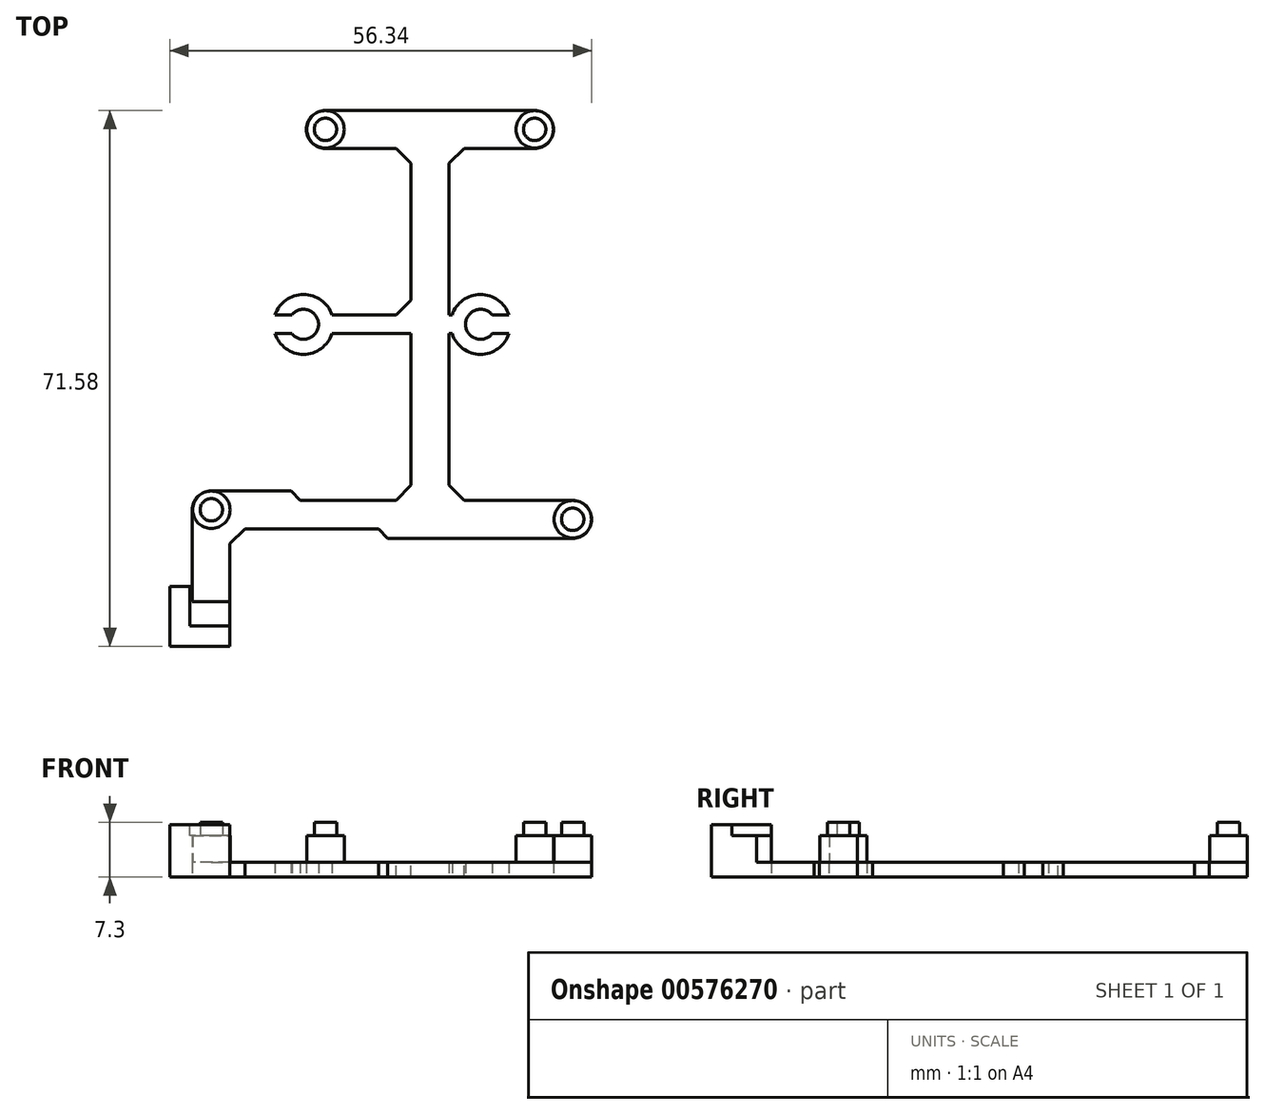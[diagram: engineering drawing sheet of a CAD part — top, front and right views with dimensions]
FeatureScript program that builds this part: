
annotation { "Feature Type Name" : "Feature", "Feature Type Description" : "" }
export const myFeature = defineFeature(function(context is Context, id is Id, definition is map)
    precondition{}
    {
        {
            var Q0;
            Q0=qCreatedBy(makeId("Top.planeOp"),FACE);
            var sketch = newSketch(context, id + "F0", { "sketchPlane" : qUnion([Q0])});
            skCircle(sketch, "E0", {"center": v(0, 0) * mm, "radius": 1.5 * mm, "construction": true});
            skLineSegment(sketch, "E1", {"start": v(2.46, -2.54) * mm, "end": v(2.46, -15.24) * mm});
            skLineSegment(sketch, "E2", {"start": v(2.46, -15.24) * mm, "end": v(-2.54, -15.24) * mm});
            skLineSegment(sketch, "E3", {"start": v(-2.54, -15.24) * mm, "end": v(-2.54, 0) * mm});
            skArc(sketch, "E4", {"start": v(0, 2.54) * mm, "mid": v(-1.8, 1.8) * mm, "end": v(-2.54, 0) * mm});
            skLineSegment(sketch, "E5", {"start": v(-2.54, -15.24) * mm, "end": v(-2.54, 45.8) * mm, "construction": true});
            skCircle(sketch, "E6", {"center": v(48.26, -1.27) * mm, "radius": 1.5 * mm, "construction": true});
            skCircle(sketch, "E7", {"center": v(15.24, 50.8) * mm, "radius": 1.5 * mm, "construction": true});
            skCircle(sketch, "E8", {"center": v(43.18, 50.8) * mm, "radius": 1.5 * mm, "construction": true});
            skLineSegment(sketch, "E9", {"start": v(15.24, 50.8) * mm, "end": v(43.18, 50.8) * mm, "construction": true});
            skArc(sketch, "E10", {"start": v(48.26, -3.8) * mm, "mid": v(50.8, -1.27) * mm, "end": v(48.26, 1.27) * mm});
            skLineSegment(sketch, "E11", {"start": v(0, 2.54) * mm, "end": v(10.66, 2.54) * mm});
            skLineSegment(sketch, "E12", {"start": v(48.26, 1.27) * mm, "end": v(31.75, 1.27) * mm});
            skLineSegment(sketch, "E13", {"start": v(10.66, 2.54) * mm, "end": v(11.85, 1.27) * mm});
            skLineSegment(sketch, "E14.0", {"start": v(22.36, -2.54) * mm, "end": v(23.55, -3.8) * mm});
            skLineSegment(sketch, "E14.1", {"start": v(48.26, -3.8) * mm, "end": v(23.55, -3.8) * mm});
            skLineSegment(sketch, "E15", {"start": v(22.36, -2.54) * mm, "end": v(2.46, -2.54) * mm});
            skLineSegment(sketch, "E16", {"start": v(29.21, 50.8) * mm, "end": v(29.21, -4.9) * mm, "construction": true});
            skArc(sketch, "E17", {"start": v(15.24, 53.34) * mm, "mid": v(12.7, 50.8) * mm, "end": v(15.24, 48.26) * mm});
            skArc(sketch, "E18", {"start": v(43.18, 48.26) * mm, "mid": v(45.72, 50.8) * mm, "end": v(43.18, 53.34) * mm});
            skLineSegment(sketch, "E19", {"start": v(15.24, 53.34) * mm, "end": v(43.18, 53.34) * mm});
            skLineSegment(sketch, "E20", {"start": v(26.67, 48.26) * mm, "end": v(26.67, 1.27) * mm});
            skLineSegment(sketch, "E21.MirrorCS", {"start": v(31.75, 48.26) * mm, "end": v(31.75, 1.27) * mm});
            skLineSegment(sketch, "E22", {"start": v(15.24, 48.26) * mm, "end": v(26.67, 48.26) * mm});
            skPoint(sketch, "E23.orphan", {"position": v(26.67, 50.02) * mm});
            skPoint(sketch, "E24.orphan", {"position": v(31.75, 50.02) * mm});
            skLineSegment(sketch, "E25.trimOffspring", {"start": v(31.75, 48.26) * mm, "end": v(43.18, 48.26) * mm});
            skPoint(sketch, "E26.orphan", {"position": v(26.67, 1.3) * mm});
            skLineSegment(sketch, "E27.trimOffspring", {"start": v(26.67, 1.27) * mm, "end": v(11.85, 1.27) * mm});
            skPoint(sketch, "E28.orphan", {"position": v(31.75, 1.3) * mm});
            skSolve(sketch);
        }
        {
            var Q0;
            Q0=makeQuery(id+"F0.imprint","IMPRINT",FACE,{"disambiguationData":[TD([[makeQuery(id+"F0.imprint","IMPRINT",EDGE,{"derivedFrom":sQuery(id+"F0.wireOp",EDGE,"E0")}),-1.0]])]});
            var Q1;
            Q1=makeQuery(id+"F0.imprint","IMPRINT",FACE,{"disambiguationData":[TD([[makeQuery(id+"F0.imprint","IMPRINT",EDGE,{"derivedFrom":sQuery(id+"F0.wireOp",EDGE,"jqxbBATG-ABpr-iL7b-bOAr-Zq2woUx4JpKi")}),1.0]])]});
            var Q2;
            Q2=makeQuery(id+"F0.imprint","IMPRINT",FACE,{"disambiguationData":[TD([[makeQuery(id+"F0.imprint","IMPRINT",EDGE,{"derivedFrom":sQuery(id+"F0.wireOp",EDGE,"E1")}),-1.0]])]});
            extrude(context, id + "F1", {"entities" : qUnion([Q0, Q1, Q2]), "depth" : 2 * mm, "offsetDistance" : 25 * mm});
        }
        {
            var Q0;
            Q0=qCreatedBy(makeId("Top.planeOp"),FACE);
            var sketch = newSketch(context, id + "F2", { "sketchPlane" : qUnion([Q0])});
            skLineSegment(sketch, "E29.0", {"start": v(-2.54, -15.24) * mm, "end": v(-2.54, 0) * mm, "construction": true});
            skLineSegment(sketch, "E30.0", {"start": v(2.46, -15.24) * mm, "end": v(-2.54, -15.24) * mm});
            skLineSegment(sketch, "E31", {"start": v(-2.54, -15.24) * mm, "end": v(-2.54, -10.24) * mm});
            skLineSegment(sketch, "E32", {"start": v(-2.54, -10.24) * mm, "end": v(-5.54, -10.24) * mm});
            skLineSegment(sketch, "E33", {"start": v(-5.54, -10.24) * mm, "end": v(-5.54, -18.24) * mm});
            skLineSegment(sketch, "E34", {"start": v(-5.54, -18.24) * mm, "end": v(2.46, -18.24) * mm});
            skLineSegment(sketch, "E35", {"start": v(2.46, -15.24) * mm, "end": v(2.46, -18.24) * mm});
            skSolve(sketch);
        }
        {
            var Q0;
            Q0=makeQuery(id+"F2.imprint","IMPRINT",FACE,{"disambiguationData":[TD([[makeQuery(id+"F2.imprint","IMPRINT",EDGE,{"derivedFrom":sQuery(id+"F2.wireOp",EDGE,"E30.0")}),1.0]])]});
            extrude(context, id + "F3", {"entities" : qUnion([Q0]), "operationType" : NewBodyOperationType.ADD, "depth" : 7 * mm, "offsetDistance" : 25 * mm});
        }
        {
            var Q0;
            Q0=qCreatedBy(makeId("Top.planeOp"),FACE);
            var sketch = newSketch(context, id + "F4", { "sketchPlane" : qUnion([Q0])});
            skCircle(sketch, "E36.0", {"center": v(0, 0) * mm, "radius": 1.5 * mm, "construction": true});
            skCircle(sketch, "E37.0", {"center": v(48.26, -1.27) * mm, "radius": 1.5 * mm, "construction": true});
            skCircle(sketch, "E38.0", {"center": v(43.18, 50.8) * mm, "radius": 1.5 * mm, "construction": true});
            skCircle(sketch, "E39.0", {"center": v(15.24, 50.8) * mm, "radius": 1.5 * mm, "construction": true});
            skCircle(sketch, "E40", {"center": v(0, 0) * mm, "radius": 2.5 * mm});
            skCircle(sketch, "E41", {"center": v(48.26, -1.27) * mm, "radius": 2.5 * mm});
            skCircle(sketch, "E42", {"center": v(15.24, 50.8) * mm, "radius": 2.5 * mm});
            skCircle(sketch, "E43", {"center": v(43.18, 50.8) * mm, "radius": 2.5 * mm});
            skLineSegment(sketch, "E44.0", {"start": v(-2.54, -15.24) * mm, "end": v(-2.54, -10.24) * mm, "construction": true});
            skLineSegment(sketch, "E45.0", {"start": v(2.46, -15.24) * mm, "end": v(-2.54, -15.24) * mm, "construction": true});
            skLineSegment(sketch, "E46.bottom", {"start": v(-2.54, -15.24) * mm, "end": v(2.46, -15.24) * mm});
            skLineSegment(sketch, "E46.top", {"start": v(-2.54, -12.24) * mm, "end": v(2.46, -12.24) * mm});
            skLineSegment(sketch, "E46.left", {"start": v(-2.54, -15.24) * mm, "end": v(-2.54, -12.24) * mm});
            skLineSegment(sketch, "E46.right", {"start": v(2.46, -15.24) * mm, "end": v(2.46, -12.24) * mm});
            skSolve(sketch);
        }
        {
            var Q0;
            Q0 = qSketchRegion(id + "F4", true);
            extrude(context, id + "F5", {"entities" : qUnion([Q0]), "operationType" : NewBodyOperationType.ADD, "depth" : 5.5 * mm, "offsetDistance" : 25 * mm});
        }
        {
            var Q0;
            Q0=makeQuery(id+"F5.opExtrude","CAP_FACE",FACE,{"disambiguationData":[OSD([sQuery(id+"F4.wireOp",EDGE,"E40")])],"isStart":false});
            var sketch = newSketch(context, id + "F6", { "sketchPlane" : qUnion([Q0])});
            skCircle(sketch, "E47.0", {"center": v(0, 0) * mm, "radius": 2.5 * mm, "construction": true});
            skCircle(sketch, "E48.0", {"center": v(48.26, -1.27) * mm, "radius": 2.5 * mm, "construction": true});
            skCircle(sketch, "E49.0", {"center": v(15.24, 50.8) * mm, "radius": 2.5 * mm, "construction": true});
            skCircle(sketch, "E50.0", {"center": v(43.18, 50.8) * mm, "radius": 2.5 * mm, "construction": true});
            skCircle(sketch, "E51", {"center": v(0, 0) * mm, "radius": 1.5 * mm});
            skCircle(sketch, "E52", {"center": v(48.26, -1.27) * mm, "radius": 1.5 * mm});
            skCircle(sketch, "E53", {"center": v(15.24, 50.8) * mm, "radius": 1.5 * mm});
            skCircle(sketch, "E54", {"center": v(43.18, 50.8) * mm, "radius": 1.5 * mm});
            skSolve(sketch);
        }
        {
            var Q0;
            Q0 = qSketchRegion(id + "F6", true);
            extrude(context, id + "F7", {"entities" : qUnion([Q0]), "operationType" : NewBodyOperationType.ADD, "depth" : 1.8 * mm, "offsetDistance" : 25 * mm});
        }
        {
            var Q0;
            Q0=makeQuery(id+"F3.opExtrude","CAP_FACE",FACE,{"disambiguationData":[OSD([sQuery(id+"F2.wireOp",EDGE,"E30.0"),sQuery(id+"F2.wireOp",EDGE,"E31"),sQuery(id+"F2.wireOp",EDGE,"E32"),sQuery(id+"F2.wireOp",EDGE,"E33"),sQuery(id+"F2.wireOp",EDGE,"E34"),sQuery(id+"F2.wireOp",EDGE,"E35")])],"isStart":false});
            var sketch = newSketch(context, id + "F8", { "sketchPlane" : qUnion([Q0])});
            skLineSegment(sketch, "E55.0", {"start": v(-2.54, -15.24) * mm, "end": v(-2.54, -10.24) * mm});
            skLineSegment(sketch, "E56.0", {"start": v(2.46, -15.24) * mm, "end": v(-2.54, -15.24) * mm});
            skLineSegment(sketch, "E57.0", {"start": v(2.46, -15.24) * mm, "end": v(2.46, -15.54) * mm});
            skLineSegment(sketch, "E58.0", {"start": v(-2.54, -10.24) * mm, "end": v(-2.84, -10.24) * mm});
            skLineSegment(sketch, "E59.0", {"start": v(-2.84, -15.54) * mm, "end": v(-2.84, -10.24) * mm});
            skLineSegment(sketch, "E59.1", {"start": v(2.46, -15.54) * mm, "end": v(-2.84, -15.54) * mm});
            skPoint(sketch, "E60.orphan", {"position": v(-5.54, -10.24) * mm});
            skPoint(sketch, "E61.orphan", {"position": v(2.46, -18.24) * mm});
            skSolve(sketch);
        }
        {
            var Q0;
            Q0=makeQuery(id+"F8.imprint","IMPRINT",FACE,{"disambiguationData":[TD([[makeQuery(id+"F8.imprint","IMPRINT",EDGE,{"derivedFrom":sQuery(id+"F8.wireOp",EDGE,"E55.0")}),1.0]])]});
            extrude(context, id + "F9", {"entities" : qUnion([Q0]), "operationType" : NewBodyOperationType.REMOVE, "oppositeDirection" : true, "depth" : 1.5 * mm, "offsetDistance" : 25 * mm});
        }
        {
            var Q0;
            Q0=makeQuery(id+"F1.opExtrude","SWEPT_EDGE",EDGE,{"disambiguationData":[OSD([sQuery(id+"F0.wireOp",EDGE,"E21.MirrorCS"),sQuery(id+"F0.wireOp",EDGE,"E25.trimOffspring")])]});
            var Q1;
            Q1=makeQuery(id+"F1.opExtrude","SWEPT_EDGE",EDGE,{"disambiguationData":[OSD([sQuery(id+"F0.wireOp",EDGE,"E20"),sQuery(id+"F0.wireOp",EDGE,"E22")])]});
            var Q2;
            Q2=makeQuery(id+"F1.opExtrude","SWEPT_EDGE",EDGE,{"disambiguationData":[OSD([sQuery(id+"F0.wireOp",EDGE,"E20"),sQuery(id+"F0.wireOp",EDGE,"E27.trimOffspring")])]});
            var Q3;
            Q3=makeQuery(id+"F1.opExtrude","SWEPT_EDGE",EDGE,{"disambiguationData":[OSD([sQuery(id+"F0.wireOp",EDGE,"E12"),sQuery(id+"F0.wireOp",EDGE,"E21.MirrorCS")])]});
            var Q4;
            Q4=makeQuery(id+"F1.opExtrude","SWEPT_EDGE",EDGE,{"disambiguationData":[OSD([sQuery(id+"F0.wireOp",EDGE,"E1"),sQuery(id+"F0.wireOp",EDGE,"E15")])]});
            chamfer(context, id + "F10", {"entities" : qUnion([Q0, Q1, Q2, Q3, Q4]), "width" : 2 * mm, "tangentPropagation" : true});
        }
        {
            var Q0;
            Q0=qCreatedBy(makeId("Top.planeOp"),FACE);
            var sketch = newSketch(context, id + "F11", { "sketchPlane" : qUnion([Q0])});
            skLineSegment(sketch, "E62.0", {"start": v(31.75, 48.26) * mm, "end": v(31.75, 1.27) * mm, "construction": true});
            skLineSegment(sketch, "E63", {"start": v(31.75, 24.77) * mm, "end": v(48.26, 24.77) * mm, "construction": true});
            skCircle(sketch, "E64.0", {"center": v(48.26, -1.27) * mm, "radius": 2.5 * mm, "construction": true});
            skLineSegment(sketch, "E65", {"start": v(48.26, -1.27) * mm, "end": v(48.26, 50.8) * mm, "construction": true});
            skLineSegment(sketch, "E66.0", {"start": v(15.24, 50.8) * mm, "end": v(43.18, 50.8) * mm, "construction": true});
            skCircle(sketch, "E67.0", {"center": v(0, 0) * mm, "radius": 2.5 * mm, "construction": true});
            skLineSegment(sketch, "E68", {"start": v(0, 0) * mm, "end": v(0, 50.8) * mm, "construction": true});
            skLineSegment(sketch, "E69", {"start": v(0, 9.85) * mm, "end": v(48.26, 9.85) * mm, "construction": true});
            skLineSegment(sketch, "E70", {"start": v(24.13, 9.85) * mm, "end": v(24.13, 46.9) * mm, "construction": true});
            skArc(sketch, "E71", {"start": v(37.51, 26.02) * mm, "mid": v(33.95, 24.77) * mm, "end": v(37.51, 23.51) * mm});
            skArc(sketch, "E72", {"start": v(39.75, 26.02) * mm, "mid": v(31.95, 24.77) * mm, "end": v(39.75, 23.51) * mm});
            skLineSegment(sketch, "E73", {"start": v(37.51, 26.02) * mm, "end": v(39.75, 26.02) * mm});
            skLineSegment(sketch, "E74.MirrorCS", {"start": v(37.51, 23.52) * mm, "end": v(39.75, 23.52) * mm});
            skPoint(sketch, "E75.orphan", {"position": v(37.06, 26.02) * mm});
            skPoint(sketch, "E76.orphan", {"position": v(37.06, 23.52) * mm});
            skPoint(sketch, "E77.orphan", {"position": v(41.31, 23.52) * mm});
            skPoint(sketch, "E78.orphan", {"position": v(41.31, 26.02) * mm});
            skArc(sketch, "E79.MirrorCS", {"start": v(8.51, 26.02) * mm, "mid": v(16.3, 24.77) * mm, "end": v(8.51, 23.52) * mm});
            skArc(sketch, "E80.MirrorCS", {"start": v(10.75, 26.02) * mm, "mid": v(14.3, 24.77) * mm, "end": v(10.75, 23.51) * mm});
            skLineSegment(sketch, "E81.MirrorCS", {"start": v(10.75, 26.02) * mm, "end": v(8.51, 26.02) * mm});
            skLineSegment(sketch, "E82.MirrorCS", {"start": v(10.75, 23.52) * mm, "end": v(8.51, 23.52) * mm});
            skLineSegment(sketch, "E83", {"start": v(31.75, 26.02) * mm, "end": v(32.15, 26.02) * mm});
            skLineSegment(sketch, "E84.0", {"start": v(26.67, 48.26) * mm, "end": v(26.67, 1.27) * mm, "construction": true});
            skLineSegment(sketch, "E85", {"start": v(16.1, 26.02) * mm, "end": v(26.67, 26.02) * mm});
            skLineSegment(sketch, "E86.MirrorCS", {"start": v(31.75, 23.52) * mm, "end": v(32.15, 23.52) * mm});
            skLineSegment(sketch, "E87.MirrorCS", {"start": v(16.1, 23.52) * mm, "end": v(26.67, 23.52) * mm});
            skLineSegment(sketch, "E88", {"start": v(26.67, 26.02) * mm, "end": v(26.67, 23.52) * mm});
            skLineSegment(sketch, "E89", {"start": v(31.75, 23.52) * mm, "end": v(31.75, 26.02) * mm});
            skPoint(sketch, "E90.orphan", {"position": v(14.35, 26.02) * mm});
            skPoint(sketch, "E91.orphan", {"position": v(14.35, 23.52) * mm});
            skPoint(sketch, "E92.orphan", {"position": v(33, 23.52) * mm});
            skPoint(sketch, "E93.orphan", {"position": v(33, 26.02) * mm});
            skSolve(sketch);
        }
        {
            var Q0;
            Q0 = qSketchRegion(id + "F11", true);
            extrude(context, id + "F12", {"entities" : qUnion([Q0]), "operationType" : NewBodyOperationType.ADD, "depth" : 2 * mm, "offsetDistance" : 25 * mm});
        }
        {
            var Q0;
            Q0=makeQuery(id+"F12.opExtrude","SWEPT_EDGE",EDGE,{"disambiguationData":[OSD([sQuery(id+"F11.wireOp",EDGE,"E87.MirrorCS"),sQuery(id+"F11.wireOp",EDGE,"E88")])]});
            var Q1;
            Q1=makeQuery(id+"F12.opExtrude","SWEPT_EDGE",EDGE,{"disambiguationData":[OSD([sQuery(id+"F11.wireOp",EDGE,"E85"),sQuery(id+"F11.wireOp",EDGE,"E88")])]});
            chamfer(context, id + "F13", {"entities" : qUnion([Q0, Q1]), "width" : 2 * mm, "tangentPropagation" : true});
        }
    });
